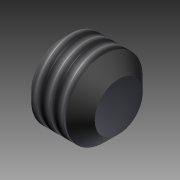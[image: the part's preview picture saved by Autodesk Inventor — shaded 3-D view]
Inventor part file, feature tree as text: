
AUTODESK INVENTOR PART (.ipt)
format: ipt  version: 2011 SP1 (Build 150282100, 282)  size: 113,152 bytes
history: native  units: mm
features: other x7, sketch x3, revolve x2, thread x1, extrude x1
ambient origin geometry x8: Origin, YZ Plane, XZ Plane, XY Plane, X Axis, Y Axis, Z Axis, Center Point
bodies: Solid1 (feature_tree)
feature tree (14):
  revolve  "Revolution1"  [1 undecoded]
  thread  "Thread1"  [1 undecoded]
  extrude  "Extrusion1"  TaperAngle=0.0deg  [1 undecoded]
  revolve  "Revolution2"  [1 undecoded]
  other  "CP_XY"
  other  "CP_YZ"
  other  "CP_ZX"
  other  "CP_X"
  other  "CP_Y"
  other  "CP_Z"
  other  "CP_Center"
  sketch  "Sketch_1"  dims[d0=360.0deg d1=1.8205mm d2=0.0mm d3=1.5mm d4=0.0mm]
  sketch  "Sketch_2"  dims[d5=360.0deg d6=0.0mm]
  sketch  "Sketch_3"
note: 4 required parameter values undecoded (feature->parameter linkage not recoverable at this tier; creation-order binding heuristic only, values carry confidence <= 0.55)